# Revit family: Storm Area Light 463055 300W
name_source: partatom
category: Lighting Fixtures
units: mm (PartAtom-declared; Revit-internal decimal feet)

## family parameters
Cut with Voids When Loaded = No
Host = Face
Light Source = Yes
Part Type = Normal
Room Calculation Point = No
Round Connector Dimension = Use Diameter
Shared = No

## types (1)
- Storm Area Light 463055 - 300W, 5000K
    1 cell = No
    2 cell = Yes
    Apparent Load = 300 VA
    Assembly Code = D5020230
    COBieBarCode = 7320043111321
    Color Filter = 16777215
    Cost = 0 $
    Default Elevation = 1219 mm
    Description = Luminaire body in white cast aluminium. Reflector in either specular or matt anodised aluminium. Specular metallised advanced Anti Glare Control ring above the LED module. Mechanical shielding 45 deg.
    Dimming Lamp Color Temperature Shift = <None>
    Emit Shape Visible in Rendering = No
    Emit from Rectangle Length = 280 mm  [stored 0.918635 ft]
    Emit from Rectangle Width = 270 mm  [stored 0.885827 ft]
    FagerhultPartNumber = 72466-365
    Height = 200 mm  [stored 0.656168 ft]
    Keynote = V59
    LOR = 100
    Lamp = 0
    Manufacturer = Fagerhult Lighting
    MaterialAccentBody = <By Category>
    MaterialBody = Default
    MaterialLouvre = <By Category>
    MaterialReflector = Default
    Model = Pleiad-SLD-G3-Surface-mounted-
    NumberOfLamps = 1
    Photometric Web File = 463055.IES
    Tilt Angle = 90.00°
    TotalLength = 180 mm  [stored 0.590551 ft]
    TotalWidth = 0 mm  [stored 0 ft]
    Type Comments = PLEIAD CMF SURF. SPEC. 4K 2000 LM DALI Body mounted with Philips Touch and Dim DALI for dimming.
    URL = www.fagerhult.se
    Weight_Kg = 6.9

note: [stored X ft] marks values corroborated as IEEE doubles in the binary element streams (Revit-internal decimal feet)

## geometry (parser evidence)
native form markers: Blend x44, Sweep x1
no freeform markers — native parametric forms only
